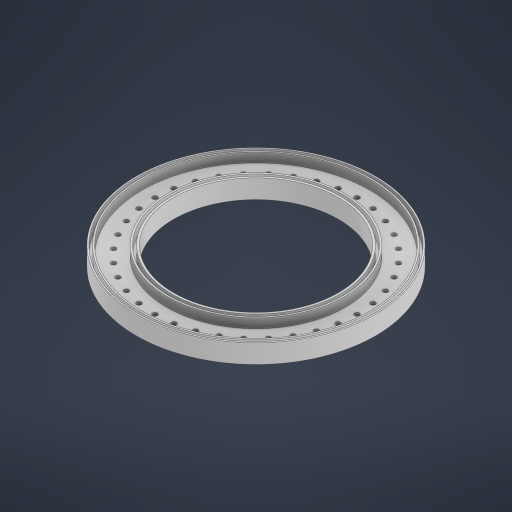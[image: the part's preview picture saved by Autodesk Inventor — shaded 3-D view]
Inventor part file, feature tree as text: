
AUTODESK INVENTOR PART (.ipt)
format: ipt  version: 2024 (Build 280153000, 153)  size: 323,584 bytes
history: native  units: mm
features: extrude x3, sketch x3, projected_geometry x1
ambient origin geometry x8: Origin, YZ Plane, XZ Plane, XY Plane, X Axis, Y Axis, Z Axis, Center Point
bodies: Solid1 (feature_tree)
feature tree (7):
  extrude  "Extrusion1"  Depth=8.0mm TaperAngle=0.0deg
  extrude  "Extrusion2"  Depth=8.0mm TaperAngle=0.0deg
  extrude  "Extrusion3"  [1 undecoded]
  sketch  "Sketch1"  dims[d0=8.0mm d1=0.0mm d2=8.0mm d3=0.0mm]
  sketch  "Sketch2"  dims[d5=360.0mm d6=145.0mm d7=200.0mm d8=360.0deg d9=8.0mm d10=0.0mm]
  sketch  "Sketch3"
  projected_geometry  "Projected Loop1"
note: 1 required parameter value undecoded (feature->parameter linkage not recoverable at this tier; creation-order binding heuristic only, values carry confidence <= 0.55)
